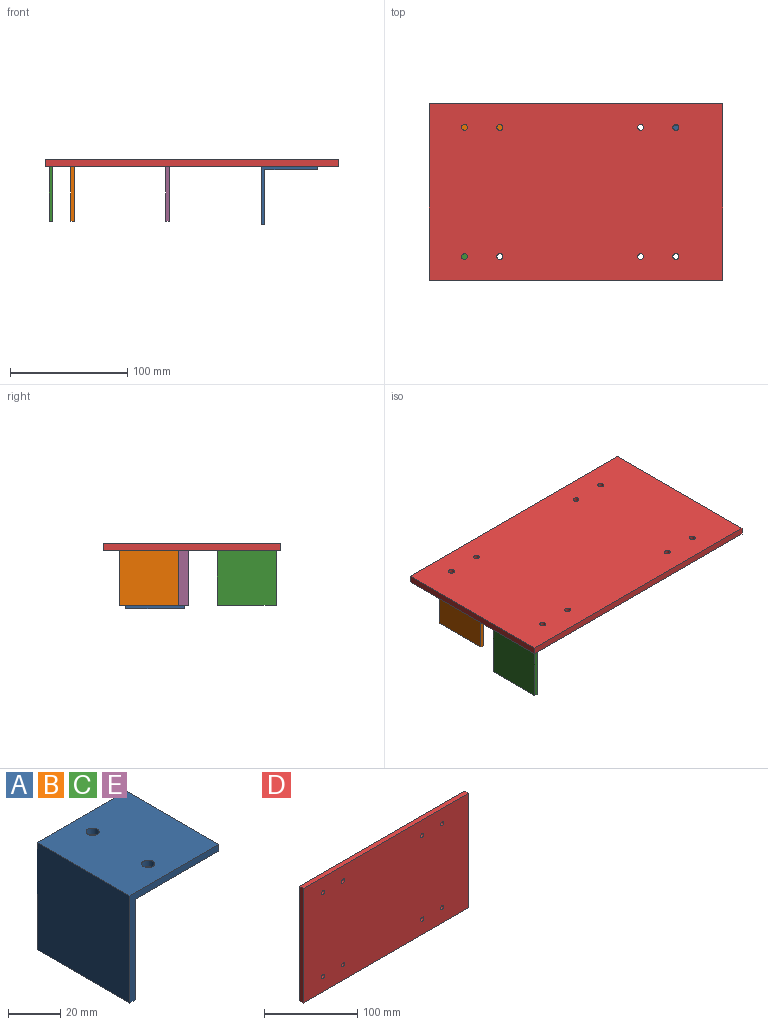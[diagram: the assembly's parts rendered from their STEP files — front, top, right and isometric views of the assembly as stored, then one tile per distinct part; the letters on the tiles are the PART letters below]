
ASSEMBLY  parts=5 mates=4
PART A: 10 faces, bbox 48.2x50x50 mm
  f0: plane 50x47mm, normal (1,0,0), area 2350mm2, adj f1,f5,f6,f7
  f1: plane 50x45mm, normal (0,0,-1), area 2210.7mm2, adj f0,f2,f6,f7,f8,f9
  f2: plane 50x3mm, normal (1,0,-0.06), area 150.3mm2, adj f1,f3,f6,f7
  f3: plane 50x48.17mm, normal (0,0,1), area 2369.4mm2, adj f2,f4,f6,f7,f8,f9
  f4: plane 50x50mm, normal (-1,0,0), area 2500mm2, adj f3,f5,f6,f7
  f5: plane 50x3mm, normal (0,0,-1), area 150mm2, adj f0,f4,f6,f7
  f6: plane 50x48.17mm, normal (0,-1,0), area 285.3mm2, adj f0,f1,f2,f3,f4,f5
  f7: plane 50x48.17mm, normal (0,1,0), area 285.3mm2, adj f0,f1,f2,f3,f4,f5
  f8: cylinder r=2.5mm len=5mm, axis (0,0,1), area 47.1mm2, adj f1,f3
  f9: cylinder r=2.5mm len=5mm, axis (0,0,1), area 47.1mm2, adj f1,f3
PART B: same geometry as A
PART C: same geometry as A
PART D: 14 faces, bbox 250x6x150 mm
  f0: plane 250x6mm, normal (0,0,1), area 1500mm2, adj f1,f10,f12,f13
  f1: plane 150x6mm, normal (-1,0,0), area 900mm2, adj f0,f2,f12,f13
  f2: plane 250x6mm, normal (0,0,-1), area 1500mm2, adj f1,f10,f12,f13
  f3: cylinder r=2.5mm len=6mm, axis (0,1,0), area 94.2mm2, adj f12,f13
  f4: cylinder r=2.5mm len=6mm, axis (0,1,0), area 94.2mm2, adj f12,f13
  f5: cylinder r=2.5mm len=6mm, axis (0,1,0), area 94.2mm2, adj f12,f13
  f6: cylinder r=2.5mm len=6mm, axis (0,1,0), area 94.2mm2, adj f12,f13
  f7: cylinder r=2.5mm len=6mm, axis (0,1,0), area 94.2mm2, adj f12,f13
  f8: cylinder r=2.5mm len=6mm, axis (0,1,0), area 94.2mm2, adj f12,f13
  f9: cylinder r=2.5mm len=6mm, axis (0,1,0), area 94.2mm2, adj f12,f13
  f10: plane 150x6mm, normal (1,0,0), area 900mm2, adj f0,f2,f12,f13
  f11: cylinder r=2.5mm len=6mm, axis (0,1,0), area 94.2mm2, adj f12,f13
  f12: plane 250x150mm, normal (0,-1,0), area 37342.9mm2, adj f0,f1,f2,f3,f4,f5,f6,f7
  f13: plane 250x150mm, normal (0,1,0), area 37342.9mm2, adj f0,f1,f2,f3,f4,f5,f6,f7
PART E: same geometry as A
PLACE A t=(121.12,-345.26,-84.41)mm
PLACE B t=(-41.14,-340.19,-81.41)mm
PLACE C t=(-59.4,-423.38,-81.41)mm
PLACE D rot(axis=(1,0,0),90deg) t=(41.1,-401.71,-58.53)mm fixed
PLACE E t=(39.72,-348.52,-81.41)mm
MATE planar E.f1 <-> D.f12  axis (0,0,-1) through (44.35,-373.52,-64.53)mm
MATE planar B.f1 <-> D.f11  axis (0,0,1) through (-14.1,-340.19,-64.53)mm
MATE planar D.f12 <-> A.f3  axis (0,0,-1) through (41.12,-401.71,-64.53)mm
MATE planar C.f1 <-> D.f12  axis (0,0,1) through (-32.37,-423.38,-64.53)mm
